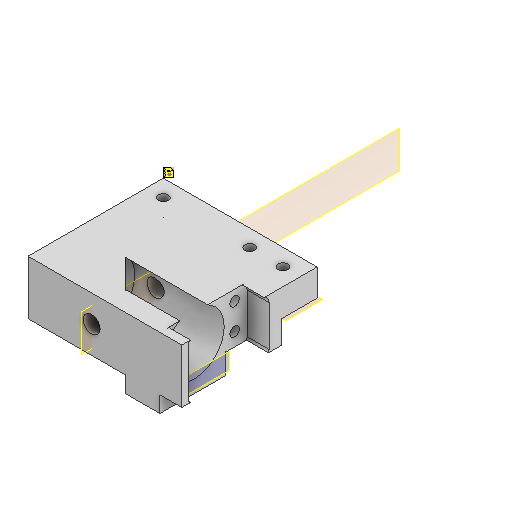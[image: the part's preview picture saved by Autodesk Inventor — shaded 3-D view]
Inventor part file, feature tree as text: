
AUTODESK INVENTOR PART (.ipt)
format: ipt  version: 2024.1 (Build 281209000, 209)  size: 382,464 bytes
history: native  units: mm
features: reference x21, extrude x14, sketch x11, plane x10, projected_geometry x7, other x6
ambient origin geometry x8: Origin, YZ Plane, XZ Plane, XY Plane, X Axis, Y Axis, Z Axis, Center Point
bodies: Body1 (feature_tree)
feature tree (69):
  plane  "Arbeitsebene6"
  extrude  "Extrusion12"  Depth=0.5mm
  extrude  "Extrusion13"  Depth=12.5mm TaperAngle=0.0deg
  plane  "Arbeitsebene7"
  extrude  "Extrusion15"  Depth=35.97mm TaperAngle=0.0deg
  plane  "Arbeitsebene8"
  plane  "Arbeitsebene9"
  plane  "Arbeitsebene10"
  sketch  "Skizze21"  dims[d75=18.0mm d76=35.97mm d77=0.0mm]
  plane  "Arbeitsebene11"
  extrude  "Extrusion18"  TaperAngle=45.0deg  [1 undecoded]
  extrude  "Extrusion19"  Depth=14.0mm TaperAngle=0.0deg
  extrude  "Extrusion20"  Depth=0.5mm
  plane  "Arbeitsebene12"
  extrude  "Extrusion22"  TaperAngle=0.0deg  [1 undecoded]
  extrude  "Extrusion23"  Depth=0.5mm
  extrude  "Extrusion27"  TaperAngle=0.0deg  [1 undecoded]
  sketch  "Skizze31"  dims[d93=20.0mm d94=0.5mm]
  plane  "Arbeitsebene13"
  extrude  "Extrusion28"  Depth=10.0mm
  extrude  "Extrusion29"  Depth=10.0mm TaperAngle=0.0deg
  sketch  "Skizze33"  dims[d107=12.0mm d108=0.0mm d109=0.0mm d110=0.0mm]
  plane  "Arbeitsebene14"
  extrude  "Extrusion30"  Depth=10.0mm TaperAngle=0.0deg
  extrude  "Extrusion31"  Depth=10.0mm
  sketch  "Skizze35"  dims[d114=0.1mm d116=10.0mm d117=0.0mm d118=10.0mm d119=0.0mm d120=6.0mm d121=9.5mm d122=9.5mm d123=2.0mm d124=2.0mm d125=2.0mm d126=2.5mm d127=10.0mm d128=0.0mm d15=0.5mm d16=0.872665mm d17=0.5mm d18=0.872665mm]
  plane  "Arbeitsebene15"
  extrude  "Extrusion32"  Depth=10.0mm
  sketch  "Skizze13"  dims[d58=8.0mm d59=0.0mm d60=0.5mm]
  reference  "Referenz11"
  reference  "Referenz12"
  reference  "Referenz13"
  reference  "Referenz14"
  sketch  "Skizze16"  dims[d62=8.0mm d63=0.0mm d66=12.5mm d67=0.0mm]
  projected_geometry  "Projizierte Kontur9"
  reference  "Referenz15"
  reference  "Referenz17"
  reference  "Referenz18"
  reference  "Referenz19"
  reference  "Referenz20"
  reference  "Referenz21"
  reference  "Referenz22"
  reference  "Referenz25"
  sketch  "Skizze22"  dims[d78=21.0mm d79=45.0deg]
  projected_geometry  "Projizierte Kontur10"
  sketch  "Skizze23"  dims[d80=1.2mm d81=14.0mm d82=0.0mm]
  projected_geometry  "Projizierte Kontur11"
  reference  "Referenz26"
  reference  "Referenz27"
  sketch  "Skizze26"  dims[d83=14.0mm d84=0.0mm d87=0.5mm]
  projected_geometry  "Projizierte Kontur13"
  sketch  "Skizze30"  dims[d88=10.0mm d89=0.0mm d90=0.0mm d91=0.0mm]
  reference  "Referenz30"
  reference  "Referenz31"
  reference  "Referenz32"
  reference  "Referenz33"
  reference  "Referenz34"
  reference  "Referenz35"
  reference  "Referenz36"
  sketch  "Skizze34"  dims[d111=10.0mm d112=0.0mm d113=0.1mm]
  projected_geometry  "Projizierte Kontur15"
  projected_geometry  "Projizierte Kontur16"
  projected_geometry  "Projizierte Kontur17"
  other  "Assemlby_lightsheet_generator_passive_v2.iam"
  other  "30_Scanlens_Laseradaper_lid_v1:1"
  other  "30_Lightsheet_generator_passive_lid_v1:1"
  other  "00_Thorlabs_LJ1878L1-A-Step:1"
  other  "00_SMAConnector_fiber copy:1"
  other  "30_Laser_to_M12Adapter:1"
note: 3 required parameter values undecoded (feature->parameter linkage not recoverable at this tier; creation-order binding heuristic only, values carry confidence <= 0.55)
